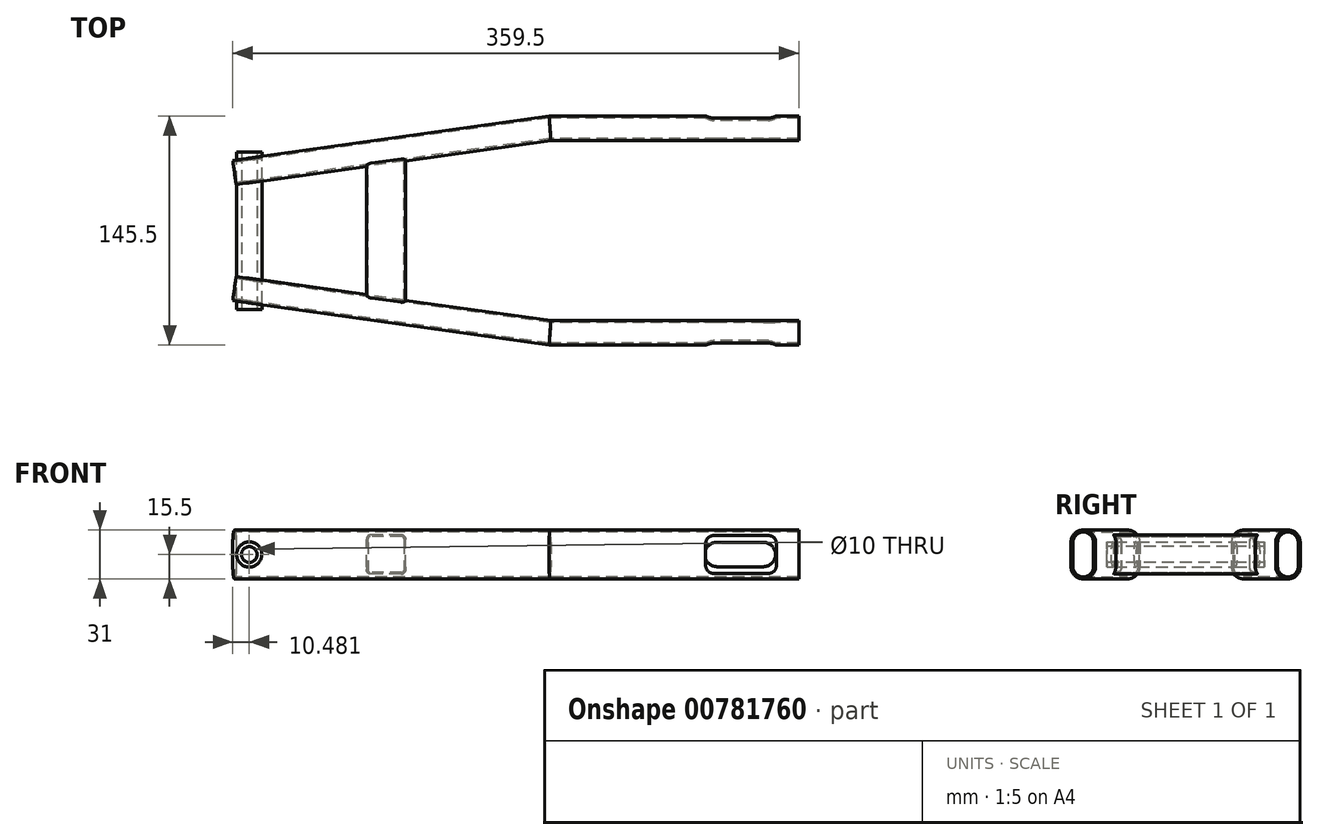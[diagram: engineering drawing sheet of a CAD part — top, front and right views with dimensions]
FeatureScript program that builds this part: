
annotation { "Feature Type Name" : "Feature", "Feature Type Description" : "" }
export const myFeature = defineFeature(function(context is Context, id is Id, definition is map)
    precondition{}
    {
        {
            var Q0;
            Q0=qCreatedBy(makeId("Top.planeOp"),FACE);
            var sketch = newSketch(context, id + "F0", { "sketchPlane" : qUnion([Q0])});
            skLineSegment(sketch, "E0", {"start": v(0, 65) * mm, "end": v(-158.03, 65) * mm});
            skLineSegment(sketch, "E1", {"start": v(-158.03, 65) * mm, "end": v(-358.42, 36.84) * mm});
            skSolve(sketch);
        }
        {
            var Q0;
            Q0=qCreatedBy(makeId("Right.planeOp"),FACE);
            var sketch = newSketch(context, id + "F1", { "sketchPlane" : qUnion([Q0])});
            skLineSegment(sketch, "E2.left", {"start": v(57.25, 7.75) * mm, "end": v(57.25, -7.75) * mm});
            skLineSegment(sketch, "E2.right", {"start": v(72.75, 7.75) * mm, "end": v(72.75, -7.75) * mm});
            skPoint(sketch, "E2.middle", {"position": v(65, 0) * mm});
            skArc(sketch, "E3", {"start": v(57.25, 7.75) * mm, "mid": v(65, 15.5) * mm, "end": v(72.75, 7.75) * mm});
            skArc(sketch, "E4", {"start": v(57.25, -7.75) * mm, "mid": v(65, -15.5) * mm, "end": v(72.75, -7.75) * mm});
            skArc(sketch, "E5.0", {"start": v(58.45, 7.75) * mm, "mid": v(65, 14.3) * mm, "end": v(71.55, 7.75) * mm});
            skLineSegment(sketch, "E6.0", {"start": v(58.45, 7.75) * mm, "end": v(58.45, -7.75) * mm});
            skLineSegment(sketch, "E7.0", {"start": v(71.55, 7.75) * mm, "end": v(71.55, -7.75) * mm});
            skArc(sketch, "E8.0", {"start": v(58.45, -7.75) * mm, "mid": v(65, -14.3) * mm, "end": v(71.55, -7.75) * mm});
            skSolve(sketch);
        }
        {
            var Q0;
            Q0=makeQuery(id+"F1.imprint","IMPRINT",FACE,{"disambiguationData":[TD([[makeQuery(id+"F1.imprint","IMPRINT",EDGE,{"derivedFrom":sQuery(id+"F1.wireOp",EDGE,"E2.left")}),1.0]])]});
            var Q1;
            Q1=sQuery(id+"F0.wireOp",EDGE,"E0");
            var Q2;
            Q2=sQuery(id+"F0.wireOp",EDGE,"E1");
            sweep(context, id + "F2", {"profiles" : qUnion([Q0]), "path" : qUnion([Q1, Q2])});
        }
        {
            var Q0;
            Q0=makeQuery(id+"F2.opSweep","SWEPT_FACE",FACE,{"disambiguationData":[OSD([sQuery(id+"F0.wireOp",EDGE,"E0"),sQuery(id+"F1.wireOp",EDGE,"E2.right")])]});
            var sketch = newSketch(context, id + "F3", { "sketchPlane" : qUnion([Q0])});
            skLineSegment(sketch, "E9.bottom", {"start": v(52.04, -7.75) * mm, "end": v(22.54, -7.75) * mm});
            skLineSegment(sketch, "E9.top", {"start": v(52.04, 7.75) * mm, "end": v(22.54, 7.75) * mm});
            skArc(sketch, "E10", {"start": v(22.54, -7.75) * mm, "mid": v(14.79, 0) * mm, "end": v(22.54, 7.75) * mm});
            skArc(sketch, "E11", {"start": v(52.04, 7.75) * mm, "mid": v(59.79, 0) * mm, "end": v(52.04, -7.75) * mm});
            skSolve(sketch);
        }
        {
            var Q0;
            Q0=makeQuery(id+"F2.opSweep","SWEPT_FACE",FACE,{"disambiguationData":[OSD([sQuery(id+"F0.wireOp",EDGE,"E0"),sQuery(id+"F1.wireOp",EDGE,"E2.left")])]});
            var sketch = newSketch(context, id + "F4", { "sketchPlane" : qUnion([Q0])});
            skArc(sketch, "E12.0", {"start": v(-52.04, 7.75) * mm, "mid": v(-59.79, 0) * mm, "end": v(-52.04, -7.75) * mm});
            skLineSegment(sketch, "E13.0", {"start": v(-52.04, 7.75) * mm, "end": v(-22.54, 7.75) * mm});
            skArc(sketch, "E14.0", {"start": v(-22.54, -7.75) * mm, "mid": v(-14.79, 0) * mm, "end": v(-22.54, 7.75) * mm});
            skLineSegment(sketch, "E15.0", {"start": v(-52.04, -7.75) * mm, "end": v(-22.54, -7.75) * mm});
            skSolve(sketch);
        }
        {
            var Q0;
            Q0=makeQuery(id+"F4.imprint","IMPRINT",FACE,{"disambiguationData":[TD([[makeQuery(id+"F4.imprint","IMPRINT",EDGE,{"derivedFrom":sQuery(id+"F4.wireOp",EDGE,"E12.0")}),1.0]])]});
            extrude(context, id + "F5", {"entities" : qUnion([Q0]), "operationType" : NewBodyOperationType.REMOVE, "oppositeDirection" : true, "depth" : 4 * mm, "offsetDistance" : 25 * mm});
        }
        {
            var Q0;
            {var subQ0=sQuery(id+"F3.wireOp",EDGE,"E11");Q0=makeQuery(id+"F3.imprint","IMPRINT",FACE,{"disambiguationData":[TD([[makeQuery(id+"F3.imprint","IMPRINT",EDGE,{"derivedFrom":subQ0}),1.0]])]});}
            var sketch = newSketch(context, id + "F6", { "sketchPlane" : qUnion([Q0])});
            skLineSegment(sketch, "E16.bottom", {"start": v(19.16, 12) * mm, "end": v(54.16, 12) * mm});
            skLineSegment(sketch, "E16.top", {"start": v(19.16, -12) * mm, "end": v(54.16, -12) * mm});
            skLineSegment(sketch, "E16.left", {"start": v(14.16, 7) * mm, "end": v(14.16, -7) * mm});
            skLineSegment(sketch, "E16.right", {"start": v(59.16, 7) * mm, "end": v(59.16, -7) * mm});
            skPoint(sketch, "E16.middle", {"position": v(36.66, 0) * mm});
            skPoint(sketch, "E17.visualSharp", {"position": v(14.16, 12) * mm});
            skArc(sketch, "E17.filletArc", {"start": v(19.16, 12) * mm, "mid": v(15.62, 10.54) * mm, "end": v(14.16, 7) * mm});
            skPoint(sketch, "E18.visualSharp", {"position": v(59.16, 12) * mm});
            skArc(sketch, "E18.filletArc", {"start": v(59.16, 7) * mm, "mid": v(57.7, 10.54) * mm, "end": v(54.16, 12) * mm});
            skPoint(sketch, "E19.visualSharp", {"position": v(59.16, -12) * mm});
            skArc(sketch, "E19.filletArc", {"start": v(54.16, -12) * mm, "mid": v(57.7, -10.54) * mm, "end": v(59.16, -7) * mm});
            skPoint(sketch, "E20.visualSharp", {"position": v(14.16, -12) * mm});
            skArc(sketch, "E20.filletArc", {"start": v(14.16, -7) * mm, "mid": v(15.62, -10.54) * mm, "end": v(19.16, -12) * mm});
            skSolve(sketch);
        }
        {
            var Q0;
            Q0 = qSketchRegion(id + "F6", true);
            extrude(context, id + "F7", {"entities" : qUnion([Q0]), "operationType" : NewBodyOperationType.REMOVE, "oppositeDirection" : true, "depth" : 4 * mm, "offsetDistance" : 25 * mm});
        }
        {
            var Q0;
            Q0=makeQuery(id+"F2.opSweep","SWEPT_BODY",BODY,{"disambiguationData":[OSD([sQuery(id+"F0.wireOp",EDGE,"E1"),sQuery(id+"F1.wireOp",EDGE,"E2.left"),sQuery(id+"F1.wireOp",EDGE,"E2.right"),sQuery(id+"F1.wireOp",EDGE,"E3"),sQuery(id+"F1.wireOp",EDGE,"E4"),sQuery(id+"F1.wireOp",EDGE,"E5.0"),sQuery(id+"F1.wireOp",EDGE,"E6.0"),sQuery(id+"F1.wireOp",EDGE,"E7.0"),sQuery(id+"F1.wireOp",EDGE,"E8.0")])]});
            var Q1;
            Q1=qCreatedBy(makeId("Front.planeOp"),FACE);
            mirror(context, id + "F8", {"entities" : qUnion([Q0]), "mirrorPlane" : qUnion([Q1])});
        }
        {
            var Q0;
            Q0=qCreatedBy(makeId("Front.planeOp"),FACE);
            var sketch = newSketch(context, id + "F9", { "sketchPlane" : qUnion([Q0])});
            skCircle(sketch, "E21", {"center": v(-349.02, 0) * mm, "radius": 8 * mm});
            skSolve(sketch);
        }
        {
            var Q0;
            Q0=makeQuery(id+"F9.imprint","IMPRINT",FACE,{"disambiguationData":[TD([[makeQuery(id+"F9.imprint","IMPRINT",EDGE,{"derivedFrom":sQuery(id+"F9.wireOp",EDGE,"E21")}),1.0]])]});
            extrude(context, id + "F10", {"entities" : qUnion([Q0]), "operationType" : NewBodyOperationType.ADD, "endBound" : BoundingType.SYMMETRIC, "depth" : 100 * mm, "offsetDistance" : 25 * mm});
        }
        {
            var Q0;
            Q0=makeQuery(id+"F10.opExtrude","CAP_FACE",FACE,{"disambiguationData":[OSD([sQuery(id+"F9.wireOp",EDGE,"E21")])],"isStart":false});
            var sketch = newSketch(context, id + "F11", { "sketchPlane" : qUnion([Q0])});
            skCircle(sketch, "E22", {"center": v(-349.02, 0) * mm, "radius": 5 * mm});
            skSolve(sketch);
        }
        {
            var Q0;
            Q0 = qSketchRegion(id + "F11", true);
            extrude(context, id + "F12", {"entities" : qUnion([Q0]), "operationType" : NewBodyOperationType.REMOVE, "endBound" : BoundingType.THROUGH_ALL, "oppositeDirection" : true, "depth" : 25 * mm, "offsetDistance" : 25 * mm});
        }
        {
            var Q0;
            Q0=qCreatedBy(makeId("Front.planeOp"),FACE);
            var sketch = newSketch(context, id + "F13", { "sketchPlane" : qUnion([Q0])});
            skLineSegment(sketch, "E23.bottom", {"start": v(-252.69, -12.5) * mm, "end": v(-271.69, -12.5) * mm});
            skLineSegment(sketch, "E23.top", {"start": v(-252.69, 12.5) * mm, "end": v(-271.69, 12.5) * mm});
            skLineSegment(sketch, "E23.left", {"start": v(-249.69, -9.5) * mm, "end": v(-249.69, 9.5) * mm});
            skLineSegment(sketch, "E23.right", {"start": v(-274.69, -9.5) * mm, "end": v(-274.69, 9.5) * mm});
            skPoint(sketch, "E23.middle", {"position": v(-262.19, 0) * mm});
            skLineSegment(sketch, "E24.bottom", {"start": v(-252.19, -11.4) * mm, "end": v(-272.19, -11.4) * mm});
            skLineSegment(sketch, "E24.top", {"start": v(-252.19, 11.4) * mm, "end": v(-272.19, 11.4) * mm});
            skLineSegment(sketch, "E24.left", {"start": v(-250.79, -10) * mm, "end": v(-250.79, 10) * mm});
            skLineSegment(sketch, "E24.right", {"start": v(-273.59, -10) * mm, "end": v(-273.59, 10) * mm});
            skPoint(sketch, "E25.visualSharp", {"position": v(-274.69, 12.5) * mm});
            skArc(sketch, "E25.filletArc", {"start": v(-271.69, 12.5) * mm, "mid": v(-273.81, 11.62) * mm, "end": v(-274.69, 9.5) * mm});
            skPoint(sketch, "E26.visualSharp", {"position": v(-249.69, 12.5) * mm});
            skArc(sketch, "E26.filletArc", {"start": v(-249.69, 9.5) * mm, "mid": v(-250.57, 11.62) * mm, "end": v(-252.69, 12.5) * mm});
            skPoint(sketch, "E27.visualSharp", {"position": v(-249.69, -12.5) * mm});
            skArc(sketch, "E27.filletArc", {"start": v(-252.69, -12.5) * mm, "mid": v(-250.57, -11.62) * mm, "end": v(-249.69, -9.5) * mm});
            skPoint(sketch, "E28.visualSharp", {"position": v(-274.69, -12.5) * mm});
            skArc(sketch, "E28.filletArc", {"start": v(-274.69, -9.5) * mm, "mid": v(-273.81, -11.62) * mm, "end": v(-271.69, -12.5) * mm});
            skPoint(sketch, "E29.visualSharp", {"position": v(-273.59, 11.4) * mm});
            skArc(sketch, "E29.filletArc", {"start": v(-272.19, 11.4) * mm, "mid": v(-273.18, 10.99) * mm, "end": v(-273.59, 10) * mm});
            skPoint(sketch, "E30.visualSharp", {"position": v(-250.79, 11.4) * mm});
            skArc(sketch, "E30.filletArc", {"start": v(-250.79, 10) * mm, "mid": v(-251.2, 10.99) * mm, "end": v(-252.19, 11.4) * mm});
            skPoint(sketch, "E31.visualSharp", {"position": v(-250.79, -11.4) * mm});
            skArc(sketch, "E31.filletArc", {"start": v(-252.19, -11.4) * mm, "mid": v(-251.2, -10.99) * mm, "end": v(-250.79, -10) * mm});
            skPoint(sketch, "E32.visualSharp", {"position": v(-273.59, -11.4) * mm});
            skArc(sketch, "E32.filletArc", {"start": v(-273.59, -10) * mm, "mid": v(-273.18, -10.99) * mm, "end": v(-272.19, -11.4) * mm});
            skSolve(sketch);
        }
        {
            var Q0;
            Q0 = qSketchRegion(id + "F13", true);
            extrude(context, id + "F14", {"entities" : qUnion([Q0]), "operationType" : NewBodyOperationType.ADD, "endBound" : BoundingType.UP_TO_NEXT, "depth" : 25 * mm, "offsetDistance" : 25 * mm, "hasSecondDirection" : true, "secondDirectionBound" : SecondDirectionBoundingType.UP_TO_NEXT, "secondDirectionOppositeDirection" : true, "secondDirectionDepth" : 25 * mm});
        }
    });
